# Revit family: Беседка «Айрон» Арт 14281
name_source: partatom
category: Антураж
revit_build: Autodesk Revit 2018 (Build: 20180423_1000(x64)
units: mm (PartAtom-declared; Revit-internal decimal feet)

## family parameters
Всегда вертикально = Да
Источник визуального образа = Геометрия семейства
На основе рабочей плоскости = Нет
Общий = Нет
При загрузке вырезать с полостями = Нет
Точка расчета площади = Нет

## types (2) — shared parameters
URL = https://hobbyka.ru
Артикул товара = Арт. 14281
Высота = 3525 мм
Группа модели = Навесы и беседки
Длина = 4350 мм
Изготовитель = ООО «Хоббика»
Материал изделия = Дерево, сталь, ОСБ плита, гибкая черепица
Цвет каркаса = Металл - Сталь
Цвет крыши = Крыша по умолчанию
Ширина = 4350 мм

## per-type parameters (varying)
| type | Изображение типоразмера | Лавочка | Описание | Цвет лавки |
| Модель без лавочки | Без лавки.jpeg | Нет | Беседка «Айрон», модель без лавочки | <По категории> |
| Модель с лавочкой | С лавкой.jpeg | Да | Беседка «Айрон», модель с лавочкой | Орех |
